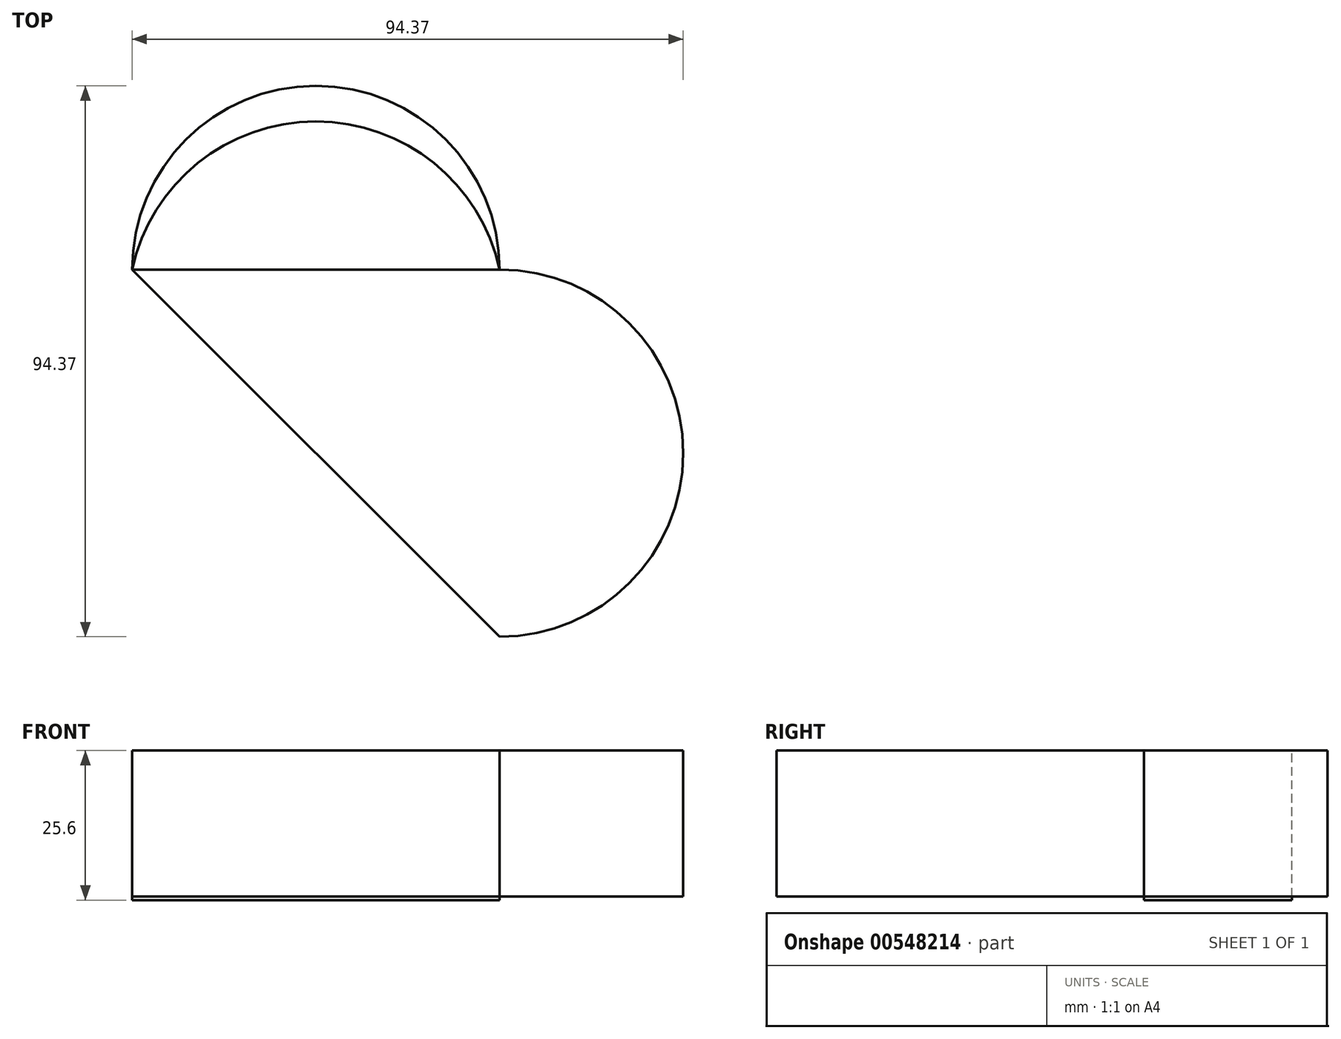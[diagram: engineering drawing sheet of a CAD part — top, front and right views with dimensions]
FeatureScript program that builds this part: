
annotation { "Feature Type Name" : "Feature", "Feature Type Description" : "" }
export const myFeature = defineFeature(function(context is Context, id is Id, definition is map)
    precondition{}
    {
        {
            var Q0;
            Q0=qCreatedBy(makeId("Top.planeOp"),FACE);
            var sketch = newSketch(context, id + "F0", { "sketchPlane" : qUnion([Q0])});
            skArc(sketch, "E0", {"start": v(0, -31.46) * mm, "mid": v(31.46, 0) * mm, "end": v(0, 31.46) * mm});
            skLineSegment(sketch, "E1", {"start": v(0, -31.46) * mm, "end": v(-31.46, 0) * mm});
            skLineSegment(sketch, "E2", {"start": v(-31.46, 0) * mm, "end": v(0, 31.46) * mm});
            skLineSegment(sketch, "E3.MirrorCS", {"start": v(-62.91, 31.46) * mm, "end": v(-31.46, 0) * mm});
            skArc(sketch, "E4.MirrorCS", {"start": v(-62.91, 31.46) * mm, "mid": v(-31.46, 62.91) * mm, "end": v(0, 31.46) * mm});
            skSolve(sketch);
        }
        {
            var Q0;
            Q0 = qSketchRegion(id + "F0", true);
            extrude(context, id + "F1", {"entities" : qUnion([Q0]), "depth" : 25 * mm, "offsetDistance" : 25 * mm});
        }
        {
            var Q0;
            Q0=makeQuery(id+"F1.opExtrude","CAP_FACE",FACE,{"disambiguationData":[OSD([sQuery(id+"F0.wireOp",EDGE,"E0"),sQuery(id+"F0.wireOp",EDGE,"E1"),sQuery(id+"F0.wireOp",EDGE,"E3.MirrorCS"),sQuery(id+"F0.wireOp",EDGE,"E4.MirrorCS")])],"isStart":false});
            var sketch = newSketch(context, id + "F2", { "sketchPlane" : qUnion([Q0])});
            skLineSegment(sketch, "E5", {"start": v(0, 31.46) * mm, "end": v(-62.91, 31.46) * mm});
            skArc(sketch, "E6", {"start": v(0, 31.46) * mm, "mid": v(-31.46, 56.81) * mm, "end": v(-62.91, 31.46) * mm});
            skSolve(sketch);
        }
        {
            var Q0;
            Q0 = qSketchRegion(id + "F2", true);
            extrude(context, id + "F3", {"entities" : qUnion([Q0]), "oppositeDirection" : true, "depth" : 25.6 * mm, "offsetDistance" : 25 * mm});
        }
    });
